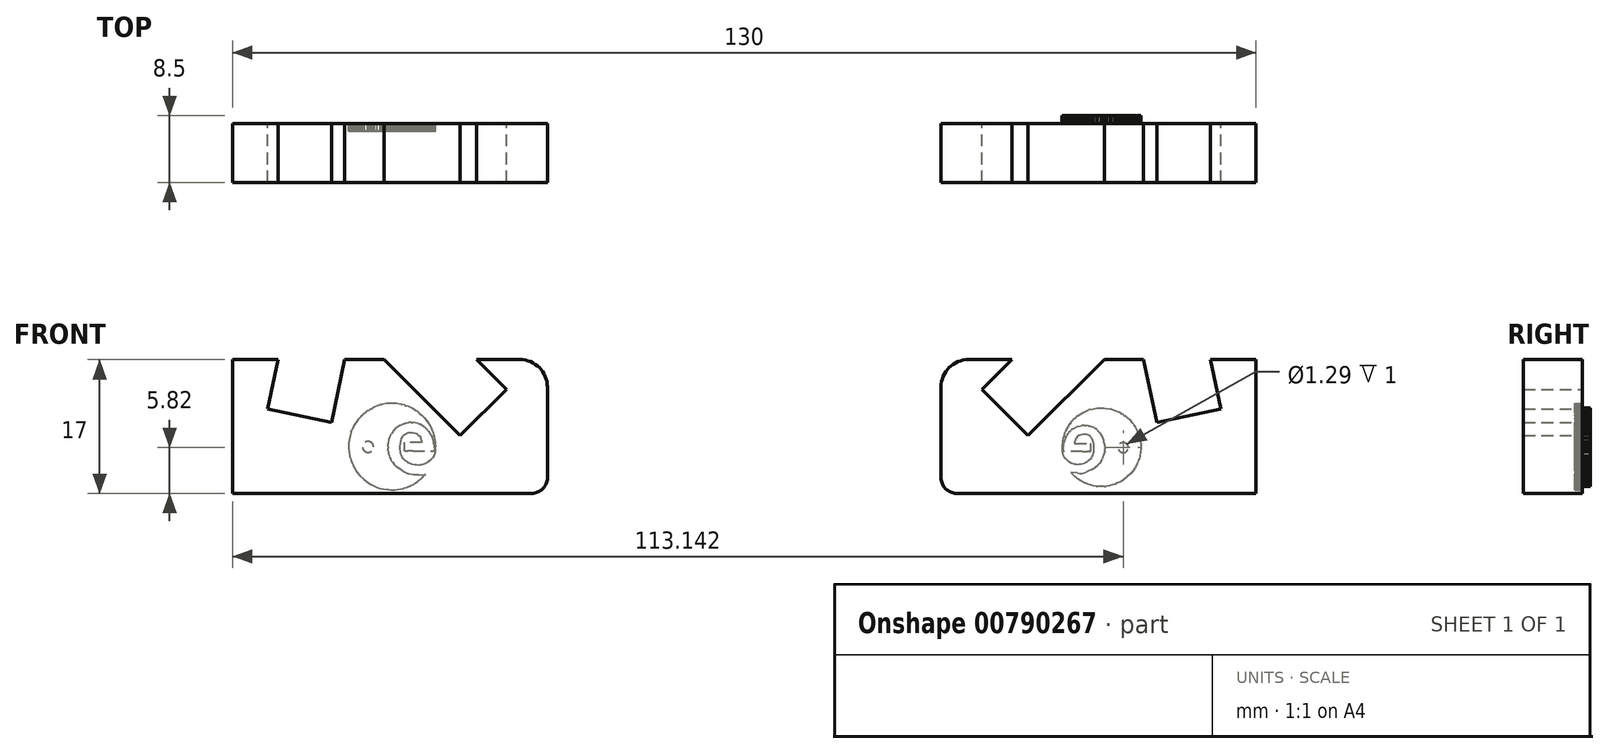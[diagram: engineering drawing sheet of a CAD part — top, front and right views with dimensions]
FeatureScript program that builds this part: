
annotation { "Feature Type Name" : "Feature", "Feature Type Description" : "" }
export const myFeature = defineFeature(function(context is Context, id is Id, definition is map)
    precondition{}
    {
        {
            var Q0;
            Q0=qCreatedBy(makeId("Front.planeOp"),FACE);
            var sketch = newSketch(context, id + "F0", { "sketchPlane" : qUnion([Q0])});
            skLineSegment(sketch, "E0", {"start": v(0, 0) * mm, "end": v(40, 0) * mm});
            skLineSegment(sketch, "E1", {"start": v(40, 0) * mm, "end": v(40, 17) * mm});
            skLineSegment(sketch, "E2", {"start": v(40, 17) * mm, "end": v(34.22, 17) * mm});
            skLineSegment(sketch, "E3", {"start": v(0, 17) * mm, "end": v(0, 0) * mm});
            skLineSegment(sketch, "E4", {"start": v(9, 17) * mm, "end": v(5.2, 13.2) * mm});
            skLineSegment(sketch, "E5", {"start": v(5.2, 13.2) * mm, "end": v(11.07, 7.33) * mm});
            skLineSegment(sketch, "E6", {"start": v(11.07, 7.33) * mm, "end": v(20.74, 17) * mm});
            skLineSegment(sketch, "E7", {"start": v(25.74, 17) * mm, "end": v(27.44, 9) * mm});
            skLineSegment(sketch, "E8", {"start": v(27.44, 9) * mm, "end": v(35.56, 10.73) * mm});
            skLineSegment(sketch, "E9", {"start": v(35.56, 10.73) * mm, "end": v(34.22, 17) * mm});
            skLineSegment(sketch, "E10.trimOffspring", {"start": v(9, 17) * mm, "end": v(0, 17) * mm});
            skLineSegment(sketch, "E11.trimOffspring", {"start": v(25.74, 17) * mm, "end": v(20.74, 17) * mm});
            skSolve(sketch);
        }
        {
            var Q0;
            Q0 = qSketchRegion(id + "F0", true);
            extrude(context, id + "F1", {"entities" : qUnion([Q0]), "depth" : 7.5 * mm, "offsetDistance" : 25 * mm});
        }
        {
            var Q0;
            Q0=makeQuery(id+"F1.opExtrude","SWEPT_EDGE",EDGE,{"disambiguationData":[OSD([sQuery(id+"F0.wireOp",EDGE,"E0"),sQuery(id+"F0.wireOp",EDGE,"E3")])]});
            fillet(context, id + "F2", {"entities" : qUnion([Q0]), "radius" : 2 * mm, "tangentPropagation" : true, "allowEdgeOverflow" : false});
        }
        {
            var Q0;
            Q0=makeQuery(id+"F1.opExtrude","SWEPT_EDGE",EDGE,{"disambiguationData":[OSD([sQuery(id+"F0.wireOp",EDGE,"E3"),sQuery(id+"F0.wireOp",EDGE,"E10.trimOffspring")])]});
            fillet(context, id + "F3", {"entities" : qUnion([Q0]), "radius" : 3.5 * mm, "tangentPropagation" : true, "allowEdgeOverflow" : false});
        }
        {
            var Q0;
            Q0=makeQuery(id+"F1.opExtrude","CAP_FACE",FACE,{"disambiguationData":[OSD([sQuery(id+"F0.wireOp",EDGE,"E0"),sQuery(id+"F0.wireOp",EDGE,"E1"),sQuery(id+"F0.wireOp",EDGE,"E2"),sQuery(id+"F0.wireOp",EDGE,"E3"),sQuery(id+"F0.wireOp",EDGE,"E4"),sQuery(id+"F0.wireOp",EDGE,"E5"),sQuery(id+"F0.wireOp",EDGE,"E6"),sQuery(id+"F0.wireOp",EDGE,"E7"),sQuery(id+"F0.wireOp",EDGE,"E8"),sQuery(id+"F0.wireOp",EDGE,"E9"),sQuery(id+"F0.wireOp",EDGE,"E10.trimOffspring"),sQuery(id+"F0.wireOp",EDGE,"E11.trimOffspring")])],"isStart":false});
            var sketch = newSketch(context, id + "F4", { "sketchPlane" : qUnion([Q0])});
            skSolve(sketch);
        }
        {
            var Q0;
            Q0=qCreatedBy(makeId("Right.planeOp"),FACE);
            cPlane(context, id + "F5", {"entities" : qUnion([Q0]), "cplaneType" : CPlaneType.OFFSET, "offset" : 25 * mm, "oppositeDirection" : true, "width" : 150 * mm, "height" : 150 * mm});
        }
        {
            var Q0;
            Q0=makeQuery(id+"F1.opExtrude","SWEPT_BODY",BODY,{"disambiguationData":[OSD([sQuery(id+"F0.wireOp",EDGE,"E0"),sQuery(id+"F0.wireOp",EDGE,"E1"),sQuery(id+"F0.wireOp",EDGE,"E2"),sQuery(id+"F0.wireOp",EDGE,"E3"),sQuery(id+"F0.wireOp",EDGE,"E4"),sQuery(id+"F0.wireOp",EDGE,"E5"),sQuery(id+"F0.wireOp",EDGE,"E6"),sQuery(id+"F0.wireOp",EDGE,"E7"),sQuery(id+"F0.wireOp",EDGE,"E8"),sQuery(id+"F0.wireOp",EDGE,"E9"),sQuery(id+"F0.wireOp",EDGE,"E10.trimOffspring"),sQuery(id+"F0.wireOp",EDGE,"E11.trimOffspring")])]});
            var Q1;
            Q1=qCreatedBy(id+"F5.planeOp",FACE);
            mirror(context, id + "F6", {"entities" : qUnion([Q0]), "mirrorPlane" : qUnion([Q1])});
        }
        {
            var Q0;
            {var subQ10=sQuery(id+"F0.wireOp",EDGE,"E1");Q0=makeQuery(id+"F4.imprint","IMPRINT",FACE,{"disambiguationData":[TD([[makeQuery(id+"F4.imprint","IMPRINT",EDGE,{"derivedFrom":makeQuery(id+"F1.opExtrude","CAP_EDGE",EDGE,{"disambiguationData":[OSD([subQ10])],"isStart":false})}),1.0]])]});}
            var sketch = newSketch(context, id + "F7", { "sketchPlane" : qUnion([Q0])});
            skLineSegment(sketch, "E12", {"start": v(15.48, 5.35) * mm, "end": v(15.48, 5.33) * mm});
            skLineSegment(sketch, "E13", {"start": v(24.52, 8.66) * mm, "end": v(24.53, 8.64) * mm});
            skLineSegment(sketch, "E14", {"start": v(24.56, 8.6) * mm, "end": v(24.53, 8.64) * mm});
            skLineSegment(sketch, "E15", {"start": v(24.56, 8.6) * mm, "end": v(24.56, 8.6) * mm});
            skLineSegment(sketch, "E16", {"start": v(24.7, 8.39) * mm, "end": v(24.78, 8.22) * mm});
            skLineSegment(sketch, "E17", {"start": v(24.56, 8.6) * mm, "end": v(24.7, 8.39) * mm});
            skLineSegment(sketch, "E18", {"start": v(24.78, 8.22) * mm, "end": v(24.8, 8.18) * mm});
            skLineSegment(sketch, "E19", {"start": v(24.8, 8.18) * mm, "end": v(24.84, 8.1) * mm});
            skLineSegment(sketch, "E20", {"start": v(24.84, 8.1) * mm, "end": v(24.9, 8) * mm});
            skLineSegment(sketch, "E21", {"start": v(24.9, 8) * mm, "end": v(24.91, 7.95) * mm});
            skLineSegment(sketch, "E22", {"start": v(24.91, 7.95) * mm, "end": v(24.95, 7.88) * mm});
            skLineSegment(sketch, "E23", {"start": v(24.95, 7.88) * mm, "end": v(24.97, 7.83) * mm});
            skLineSegment(sketch, "E24", {"start": v(25.1, 7.54) * mm, "end": v(24.97, 7.83) * mm});
            skLineSegment(sketch, "E25", {"start": v(25.1, 7.53) * mm, "end": v(25.1, 7.54) * mm});
            skLineSegment(sketch, "E26", {"start": v(25.24, 7.07) * mm, "end": v(25.33, 6.56) * mm});
            skLineSegment(sketch, "E27", {"start": v(25.1, 7.53) * mm, "end": v(25.24, 7.07) * mm});
            skLineSegment(sketch, "E28", {"start": v(25.38, 5.57) * mm, "end": v(25.36, 5.31) * mm});
            skLineSegment(sketch, "E29", {"start": v(25.38, 5.86) * mm, "end": v(25.38, 5.57) * mm});
            skLineSegment(sketch, "E30", {"start": v(25.36, 6.2) * mm, "end": v(25.38, 5.86) * mm});
            skLineSegment(sketch, "E31", {"start": v(25.33, 6.56) * mm, "end": v(25.36, 6.2) * mm});
            skLineSegment(sketch, "E32", {"start": v(25.36, 5.31) * mm, "end": v(25.24, 4.7) * mm});
            skLineSegment(sketch, "E33", {"start": v(25, 3.97) * mm, "end": v(24.9, 3.71) * mm});
            skLineSegment(sketch, "E34", {"start": v(25.1, 4.23) * mm, "end": v(25, 3.97) * mm});
            skLineSegment(sketch, "E35", {"start": v(25.18, 4.47) * mm, "end": v(25.1, 4.23) * mm});
            skLineSegment(sketch, "E36", {"start": v(25.24, 4.7) * mm, "end": v(25.18, 4.47) * mm});
            skLineSegment(sketch, "E37", {"start": v(24.9, 3.71) * mm, "end": v(24.86, 3.65) * mm});
            skLineSegment(sketch, "E38", {"start": v(23.62, 2.06) * mm, "end": v(23.08, 1.66) * mm});
            skLineSegment(sketch, "E39", {"start": v(24.1, 2.53) * mm, "end": v(23.62, 2.06) * mm});
            skLineSegment(sketch, "E40", {"start": v(24.4, 2.88) * mm, "end": v(24.1, 2.53) * mm});
            skLineSegment(sketch, "E41", {"start": v(24.64, 3.25) * mm, "end": v(24.4, 2.88) * mm});
            skLineSegment(sketch, "E42", {"start": v(24.86, 3.65) * mm, "end": v(24.64, 3.25) * mm});
            skLineSegment(sketch, "E43", {"start": v(21.36, 0.96) * mm, "end": v(20.93, 0.9) * mm});
            skLineSegment(sketch, "E44", {"start": v(21.73, 1.05) * mm, "end": v(21.36, 0.96) * mm});
            skLineSegment(sketch, "E45", {"start": v(22.09, 1.16) * mm, "end": v(21.73, 1.05) * mm});
            skLineSegment(sketch, "E46", {"start": v(22.42, 1.3) * mm, "end": v(22.09, 1.16) * mm});
            skLineSegment(sketch, "E47", {"start": v(22.76, 1.47) * mm, "end": v(22.42, 1.3) * mm});
            skLineSegment(sketch, "E48", {"start": v(23.08, 1.66) * mm, "end": v(22.76, 1.47) * mm});
            skLineSegment(sketch, "E49", {"start": v(20.77, 0.87) * mm, "end": v(20.93, 0.9) * mm});
            skLineSegment(sketch, "E50", {"start": v(20.79, 0.88) * mm, "end": v(20.77, 0.87) * mm});
            skLineSegment(sketch, "E51", {"start": v(20.79, 0.88) * mm, "end": v(20.46, 0.86) * mm});
            skLineSegment(sketch, "E52", {"start": v(20.09, 0.87) * mm, "end": v(19.8, 0.9) * mm});
            skLineSegment(sketch, "E53", {"start": v(20.46, 0.86) * mm, "end": v(20.09, 0.87) * mm});
            skLineSegment(sketch, "E54", {"start": v(19.76, 0.9) * mm, "end": v(19.8, 0.9) * mm});
            skLineSegment(sketch, "E55", {"start": v(19.76, 0.9) * mm, "end": v(19.76, 0.9) * mm});
            skLineSegment(sketch, "E56", {"start": v(19.38, 0.96) * mm, "end": v(19.02, 1.05) * mm});
            skLineSegment(sketch, "E57", {"start": v(19.76, 0.9) * mm, "end": v(19.38, 0.96) * mm});
            skLineSegment(sketch, "E58", {"start": v(18.96, 1.06) * mm, "end": v(19.02, 1.05) * mm});
            skLineSegment(sketch, "E59", {"start": v(18.96, 1.07) * mm, "end": v(18.96, 1.06) * mm});
            skLineSegment(sketch, "E60", {"start": v(18.7, 1.15) * mm, "end": v(18.44, 1.24) * mm});
            skLineSegment(sketch, "E61", {"start": v(18.96, 1.07) * mm, "end": v(18.7, 1.15) * mm});
            skLineSegment(sketch, "E62", {"start": v(18.44, 1.24) * mm, "end": v(18.41, 1.26) * mm});
            skLineSegment(sketch, "E63", {"start": v(18.41, 1.26) * mm, "end": v(18.27, 1.32) * mm});
            skLineSegment(sketch, "E64", {"start": v(18.27, 1.32) * mm, "end": v(18.25, 1.33) * mm});
            skLineSegment(sketch, "E65", {"start": v(18.25, 1.33) * mm, "end": v(18.23, 1.33) * mm});
            skLineSegment(sketch, "E66", {"start": v(18.23, 1.33) * mm, "end": v(18.15, 1.37) * mm});
            skLineSegment(sketch, "E67", {"start": v(18.15, 1.37) * mm, "end": v(17.9, 1.5) * mm});
            skLineSegment(sketch, "E68", {"start": v(17.9, 1.5) * mm, "end": v(17.89, 1.51) * mm});
            skLineSegment(sketch, "E69", {"start": v(17.89, 1.51) * mm, "end": v(17.82, 1.55) * mm});
            skLineSegment(sketch, "E70", {"start": v(17.82, 1.55) * mm, "end": v(17.78, 1.58) * mm});
            skLineSegment(sketch, "E71", {"start": v(17.78, 1.58) * mm, "end": v(17.65, 1.66) * mm});
            skLineSegment(sketch, "E72", {"start": v(17.65, 1.66) * mm, "end": v(17.4, 1.83) * mm});
            skLineSegment(sketch, "E73", {"start": v(17.28, 1.92) * mm, "end": v(17.19, 2) * mm});
            skLineSegment(sketch, "E74", {"start": v(17.4, 1.83) * mm, "end": v(17.28, 1.92) * mm});
            skLineSegment(sketch, "E75", {"start": v(17.19, 2) * mm, "end": v(17.18, 2) * mm});
            skLineSegment(sketch, "E76", {"start": v(17.05, 2.1) * mm, "end": v(16.96, 2.2) * mm});
            skLineSegment(sketch, "E77", {"start": v(17.18, 2) * mm, "end": v(17.05, 2.1) * mm});
            skLineSegment(sketch, "E78", {"start": v(16.84, 2.3) * mm, "end": v(16.96, 2.2) * mm});
            skLineSegment(sketch, "E79", {"start": v(16.85, 2.3) * mm, "end": v(16.84, 2.3) * mm});
            skLineSegment(sketch, "E80", {"start": v(16.85, 2.3) * mm, "end": v(16.67, 2.5) * mm});
            skLineSegment(sketch, "E81", {"start": v(16.66, 2.5) * mm, "end": v(16.67, 2.5) * mm});
            skLineSegment(sketch, "E82", {"start": v(16.52, 2.66) * mm, "end": v(16.66, 2.5) * mm});
            skLineSegment(sketch, "E83", {"start": v(17.31, 2.57) * mm, "end": v(16.52, 2.66) * mm});
            skLineSegment(sketch, "E84", {"start": v(18.17, 2.61) * mm, "end": v(18.48, 2.71) * mm});
            skLineSegment(sketch, "E85", {"start": v(17.9, 2.56) * mm, "end": v(18.17, 2.61) * mm});
            skLineSegment(sketch, "E86", {"start": v(17.62, 2.55) * mm, "end": v(17.9, 2.56) * mm});
            skLineSegment(sketch, "E87", {"start": v(17.31, 2.57) * mm, "end": v(17.62, 2.55) * mm});
            skLineSegment(sketch, "E88", {"start": v(19.16, 3.06) * mm, "end": v(18.48, 2.71) * mm});
            skLineSegment(sketch, "E89", {"start": v(19.16, 3.06) * mm, "end": v(19.34, 3.17) * mm});
            skLineSegment(sketch, "E90", {"start": v(19.34, 3.17) * mm, "end": v(19.55, 3.3) * mm});
            skLineSegment(sketch, "E91", {"start": v(19.55, 3.3) * mm, "end": v(19.59, 3.33) * mm});
            skLineSegment(sketch, "E92", {"start": v(19.59, 3.33) * mm, "end": v(19.59, 3.33) * mm});
            skLineSegment(sketch, "E93", {"start": v(19.59, 3.33) * mm, "end": v(19.6, 3.34) * mm});
            skLineSegment(sketch, "E94", {"start": v(19.6, 3.34) * mm, "end": v(19.6, 3.34) * mm});
            skLineSegment(sketch, "E95", {"start": v(19.84, 3.52) * mm, "end": v(20.01, 3.67) * mm});
            skLineSegment(sketch, "E96", {"start": v(19.6, 3.34) * mm, "end": v(19.84, 3.52) * mm});
            skLineSegment(sketch, "E97", {"start": v(20.01, 3.68) * mm, "end": v(20.01, 3.67) * mm});
            skLineSegment(sketch, "E98", {"start": v(20.13, 3.8) * mm, "end": v(20.01, 3.68) * mm});
            skLineSegment(sketch, "E99", {"start": v(20.32, 4.06) * mm, "end": v(20.13, 3.8) * mm});
            skLineSegment(sketch, "E100", {"start": v(20.35, 4.09) * mm, "end": v(20.32, 4.06) * mm});
            skLineSegment(sketch, "E101", {"start": v(20.35, 4.09) * mm, "end": v(20.51, 4.42) * mm});
            skLineSegment(sketch, "E102", {"start": v(20.58, 4.58) * mm, "end": v(20.51, 4.42) * mm});
            skLineSegment(sketch, "E103", {"start": v(20.58, 4.58) * mm, "end": v(20.58, 4.6) * mm});
            skLineSegment(sketch, "E104", {"start": v(20.68, 4.86) * mm, "end": v(20.74, 5.07) * mm});
            skLineSegment(sketch, "E105", {"start": v(20.58, 4.6) * mm, "end": v(20.68, 4.86) * mm});
            skLineSegment(sketch, "E106", {"start": v(20.74, 5.07) * mm, "end": v(20.75, 5.1) * mm});
            skLineSegment(sketch, "E107", {"start": v(20.8, 5.34) * mm, "end": v(20.75, 5.1) * mm});
            skLineSegment(sketch, "E108", {"start": v(20.8, 5.34) * mm, "end": v(20.83, 5.65) * mm});
            skLineSegment(sketch, "E109", {"start": v(20.83, 5.87) * mm, "end": v(20.83, 5.65) * mm});
            skLineSegment(sketch, "E110", {"start": v(20.81, 6.08) * mm, "end": v(20.79, 6.25) * mm});
            skLineSegment(sketch, "E111", {"start": v(20.83, 5.87) * mm, "end": v(20.81, 6.08) * mm});
            skLineSegment(sketch, "E112", {"start": v(20.79, 6.25) * mm, "end": v(20.79, 6.27) * mm});
            skLineSegment(sketch, "E113", {"start": v(20.79, 6.27) * mm, "end": v(20.79, 6.27) * mm});
            skLineSegment(sketch, "E114", {"start": v(20.79, 6.27) * mm, "end": v(20.71, 6.6) * mm});
            skLineSegment(sketch, "E115", {"start": v(20.71, 6.6) * mm, "end": v(20.68, 6.72) * mm});
            skLineSegment(sketch, "E116", {"start": v(20.68, 6.72) * mm, "end": v(20.57, 7.03) * mm});
            skLineSegment(sketch, "E117", {"start": v(20.48, 7.24) * mm, "end": v(20.4, 7.4) * mm});
            skLineSegment(sketch, "E118", {"start": v(20.57, 7.03) * mm, "end": v(20.48, 7.24) * mm});
            skLineSegment(sketch, "E119", {"start": v(20.27, 7.57) * mm, "end": v(20.4, 7.4) * mm});
            skLineSegment(sketch, "E120", {"start": v(20.27, 7.58) * mm, "end": v(20.27, 7.57) * mm});
            skLineSegment(sketch, "E121", {"start": v(20.17, 7.7) * mm, "end": v(20.08, 7.8) * mm});
            skLineSegment(sketch, "E122", {"start": v(20.27, 7.58) * mm, "end": v(20.17, 7.7) * mm});
            skLineSegment(sketch, "E123", {"start": v(20.08, 7.8) * mm, "end": v(19.88, 8) * mm});
            skLineSegment(sketch, "E124", {"start": v(19.78, 8.1) * mm, "end": v(19.88, 8) * mm});
            skLineSegment(sketch, "E125", {"start": v(19.78, 8.1) * mm, "end": v(19.59, 8.25) * mm});
            skLineSegment(sketch, "E126", {"start": v(19.5, 8.3) * mm, "end": v(19.59, 8.25) * mm});
            skLineSegment(sketch, "E127", {"start": v(19.27, 6.78) * mm, "end": v(19.25, 6.8) * mm});
            skLineSegment(sketch, "E128", {"start": v(19.25, 6.8) * mm, "end": v(19.17, 6.97) * mm});
            skLineSegment(sketch, "E129", {"start": v(19.17, 6.97) * mm, "end": v(19.07, 7.12) * mm});
            skLineSegment(sketch, "E130", {"start": v(19.07, 7.12) * mm, "end": v(18.95, 7.24) * mm});
            skLineSegment(sketch, "E131", {"start": v(18.95, 7.24) * mm, "end": v(18.8, 7.34) * mm});
            skLineSegment(sketch, "E132", {"start": v(18.8, 7.34) * mm, "end": v(18.65, 7.41) * mm});
            skLineSegment(sketch, "E133", {"start": v(18.65, 7.41) * mm, "end": v(18.48, 7.46) * mm});
            skLineSegment(sketch, "E134", {"start": v(18.48, 7.46) * mm, "end": v(18.11, 7.5) * mm});
            skLineSegment(sketch, "E135", {"start": v(18.11, 7.5) * mm, "end": v(18.06, 7.5) * mm});
            skLineSegment(sketch, "E136", {"start": v(18.06, 7.5) * mm, "end": v(18, 7.5) * mm});
            skLineSegment(sketch, "E137", {"start": v(18, 7.5) * mm, "end": v(17.78, 7.45) * mm});
            skLineSegment(sketch, "E138", {"start": v(17.78, 7.45) * mm, "end": v(17.57, 7.37) * mm});
            skLineSegment(sketch, "E139", {"start": v(17.57, 7.37) * mm, "end": v(17.55, 7.36) * mm});
            skLineSegment(sketch, "E140", {"start": v(17.55, 7.36) * mm, "end": v(17.55, 7.36) * mm});
            skLineSegment(sketch, "E141", {"start": v(17.55, 7.36) * mm, "end": v(17.35, 7.23) * mm});
            skLineSegment(sketch, "E142", {"start": v(17.35, 7.23) * mm, "end": v(17.2, 7.07) * mm});
            skLineSegment(sketch, "E143", {"start": v(17.2, 7.07) * mm, "end": v(17.08, 6.89) * mm});
            skLineSegment(sketch, "E144", {"start": v(17.08, 6.89) * mm, "end": v(17.08, 6.88) * mm});
            skLineSegment(sketch, "E145", {"start": v(17.08, 6.88) * mm, "end": v(17.05, 6.82) * mm});
            skLineSegment(sketch, "E146", {"start": v(17.05, 6.82) * mm, "end": v(17, 6.68) * mm});
            skLineSegment(sketch, "E147", {"start": v(17, 6.68) * mm, "end": v(17, 6.68) * mm});
            skLineSegment(sketch, "E148", {"start": v(17, 6.68) * mm, "end": v(16.96, 6.5) * mm});
            skLineSegment(sketch, "E149", {"start": v(16.96, 6.5) * mm, "end": v(16.95, 6.5) * mm});
            skLineSegment(sketch, "E150", {"start": v(16.95, 6.66) * mm, "end": v(16.95, 6.33) * mm});
            skLineSegment(sketch, "E151", {"start": v(16.95, 6.33) * mm, "end": v(18.98, 6.33) * mm});
            skLineSegment(sketch, "E152", {"start": v(18.98, 6.33) * mm, "end": v(18.98, 5.33) * mm});
            skLineSegment(sketch, "E153", {"start": v(18.88, 5.33) * mm, "end": v(18.98, 5.33) * mm});
            skLineSegment(sketch, "E154", {"start": v(18.88, 5.33) * mm, "end": v(18.57, 5.33) * mm});
            skLineSegment(sketch, "E155", {"start": v(18.57, 5.33) * mm, "end": v(18.57, 5.33) * mm});
            skLineSegment(sketch, "E156", {"start": v(17.99, 5.33) * mm, "end": v(18.57, 5.33) * mm});
            skLineSegment(sketch, "E157", {"start": v(17.99, 5.33) * mm, "end": v(18, 5.33) * mm});
            skLineSegment(sketch, "E158", {"start": v(18, 5.33) * mm, "end": v(15.48, 5.33) * mm});
            skLineSegment(sketch, "E159", {"start": v(15.48, 5.35) * mm, "end": v(15.47, 5.55) * mm});
            skLineSegment(sketch, "E160", {"start": v(15.5, 5.81) * mm, "end": v(15.48, 5.66) * mm});
            skLineSegment(sketch, "E161", {"start": v(15.48, 5.66) * mm, "end": v(15.47, 5.55) * mm});
            skLineSegment(sketch, "E162", {"start": v(15.53, 6.08) * mm, "end": v(15.5, 5.81) * mm});
            skLineSegment(sketch, "E163", {"start": v(15.53, 6.08) * mm, "end": v(15.53, 6.08) * mm});
            skLineSegment(sketch, "E164", {"start": v(15.53, 6.08) * mm, "end": v(15.56, 6.27) * mm});
            skLineSegment(sketch, "E165", {"start": v(15.58, 6.33) * mm, "end": v(15.56, 6.27) * mm});
            skLineSegment(sketch, "E166", {"start": v(15.62, 6.5) * mm, "end": v(15.58, 6.33) * mm});
            skLineSegment(sketch, "E167", {"start": v(15.65, 6.58) * mm, "end": v(15.62, 6.5) * mm});
            skLineSegment(sketch, "E168", {"start": v(15.65, 6.6) * mm, "end": v(15.65, 6.58) * mm});
            skLineSegment(sketch, "E169", {"start": v(15.65, 6.6) * mm, "end": v(15.65, 6.6) * mm});
            skLineSegment(sketch, "E170", {"start": v(15.66, 6.64) * mm, "end": v(15.65, 6.6) * mm});
            skLineSegment(sketch, "E171", {"start": v(15.67, 6.65) * mm, "end": v(15.66, 6.64) * mm});
            skLineSegment(sketch, "E172", {"start": v(15.7, 6.73) * mm, "end": v(15.67, 6.65) * mm});
            skLineSegment(sketch, "E173", {"start": v(15.77, 6.96) * mm, "end": v(15.72, 6.83) * mm});
            skLineSegment(sketch, "E174", {"start": v(15.72, 6.83) * mm, "end": v(15.7, 6.73) * mm});
            skLineSegment(sketch, "E175", {"start": v(15.77, 6.96) * mm, "end": v(15.77, 6.96) * mm});
            skLineSegment(sketch, "E176", {"start": v(18.2, 8.64) * mm, "end": v(18.2, 8.64) * mm});
            skLineSegment(sketch, "E177", {"start": v(24.25, 9.02) * mm, "end": v(24.26, 9) * mm});
            skLineSegment(sketch, "E178", {"start": v(18.2, 8.64) * mm, "end": v(18.45, 8.63) * mm});
            skLineSegment(sketch, "E179", {"start": v(24.25, 9.02) * mm, "end": v(24.25, 9.02) * mm});
            skLineSegment(sketch, "E180", {"start": v(18.72, 8.58) * mm, "end": v(18.45, 8.63) * mm});
            skLineSegment(sketch, "E181", {"start": v(24.25, 9.02) * mm, "end": v(24.18, 9.1) * mm});
            skLineSegment(sketch, "E182", {"start": v(18.72, 8.58) * mm, "end": v(18.88, 8.54) * mm});
            skLineSegment(sketch, "E183", {"start": v(23.91, 9.39) * mm, "end": v(24.18, 9.1) * mm});
            skLineSegment(sketch, "E184", {"start": v(19.2, 8.43) * mm, "end": v(18.99, 8.51) * mm});
            skLineSegment(sketch, "E185", {"start": v(23.91, 9.39) * mm, "end": v(23.92, 9.4) * mm});
            skLineSegment(sketch, "E186", {"start": v(23.92, 9.4) * mm, "end": v(23.8, 9.5) * mm});
            skLineSegment(sketch, "E187", {"start": v(24.4, 8.81) * mm, "end": v(24.52, 8.66) * mm});
            skLineSegment(sketch, "E188", {"start": v(19.5, 8.3) * mm, "end": v(19.34, 8.38) * mm});
            skLineSegment(sketch, "E189", {"start": v(23.56, 9.7) * mm, "end": v(23.7, 9.6) * mm});
            skLineSegment(sketch, "E190", {"start": v(23.7, 9.6) * mm, "end": v(23.8, 9.5) * mm});
            skLineSegment(sketch, "E191", {"start": v(23.54, 9.71) * mm, "end": v(23.56, 9.7) * mm});
            skLineSegment(sketch, "E192", {"start": v(23.54, 9.71) * mm, "end": v(23.54, 9.71) * mm});
            skLineSegment(sketch, "E193", {"start": v(23.54, 9.71) * mm, "end": v(23.35, 9.85) * mm});
            skLineSegment(sketch, "E194", {"start": v(22.6, 10.33) * mm, "end": v(22.6, 10.33) * mm});
            skLineSegment(sketch, "E195", {"start": v(22.12, 10.54) * mm, "end": v(22.4, 10.43) * mm});
            skLineSegment(sketch, "E196", {"start": v(21.6, 10.7) * mm, "end": v(22.12, 10.54) * mm});
            skLineSegment(sketch, "E197", {"start": v(22.8, 10.22) * mm, "end": v(22.6, 10.33) * mm});
            skLineSegment(sketch, "E198", {"start": v(22.8, 10.22) * mm, "end": v(22.8, 10.22) * mm});
            skLineSegment(sketch, "E199", {"start": v(22.8, 10.22) * mm, "end": v(22.99, 10.1) * mm});
            skLineSegment(sketch, "E200", {"start": v(23.18, 10) * mm, "end": v(22.99, 10.1) * mm});
            skLineSegment(sketch, "E201", {"start": v(23.18, 9.98) * mm, "end": v(23.18, 10) * mm});
            skLineSegment(sketch, "E202", {"start": v(23.18, 9.98) * mm, "end": v(23.35, 9.85) * mm});
            skLineSegment(sketch, "E203", {"start": v(18.99, 8.51) * mm, "end": v(18.88, 8.54) * mm});
            skLineSegment(sketch, "E204", {"start": v(24.26, 9) * mm, "end": v(24.4, 8.81) * mm});
            skLineSegment(sketch, "E205", {"start": v(18.2, 8.64) * mm, "end": v(17.93, 8.63) * mm});
            skLineSegment(sketch, "E206", {"start": v(22.4, 10.43) * mm, "end": v(22.6, 10.33) * mm});
            skCircle(sketch, "E207", {"center": v(23.14, 5.82) * mm, "radius": 0.64 * mm});
            skLineSegment(sketch, "E208", {"start": v(19.18, 4.64) * mm, "end": v(19.29, 4.85) * mm});
            skLineSegment(sketch, "E209", {"start": v(17.39, 8.52) * mm, "end": v(17.93, 8.63) * mm});
            skLineSegment(sketch, "E210", {"start": v(17.39, 8.52) * mm, "end": v(17.2, 8.45) * mm});
            skLineSegment(sketch, "E211", {"start": v(16.73, 8.2) * mm, "end": v(17.2, 8.45) * mm});
            skLineSegment(sketch, "E212", {"start": v(16.6, 8.1) * mm, "end": v(16.5, 8.02) * mm});
            skLineSegment(sketch, "E213", {"start": v(16.73, 8.2) * mm, "end": v(16.6, 8.1) * mm});
            skLineSegment(sketch, "E214", {"start": v(16.3, 7.84) * mm, "end": v(16.5, 8.02) * mm});
            skLineSegment(sketch, "E215", {"start": v(16.3, 7.84) * mm, "end": v(16.3, 7.84) * mm});
            skLineSegment(sketch, "E216", {"start": v(16.3, 7.84) * mm, "end": v(16.27, 7.8) * mm});
            skLineSegment(sketch, "E217", {"start": v(16.18, 7.68) * mm, "end": v(16.12, 7.6) * mm});
            skLineSegment(sketch, "E218", {"start": v(16.27, 7.8) * mm, "end": v(16.18, 7.68) * mm});
            skLineSegment(sketch, "E219", {"start": v(16.12, 7.6) * mm, "end": v(15.96, 7.33) * mm});
            skLineSegment(sketch, "E220", {"start": v(15.87, 7.17) * mm, "end": v(15.96, 7.33) * mm});
            skLineSegment(sketch, "E221", {"start": v(15.87, 7.17) * mm, "end": v(15.86, 7.15) * mm});
            skLineSegment(sketch, "E222", {"start": v(15.86, 7.15) * mm, "end": v(15.77, 6.96) * mm});
            skLineSegment(sketch, "E223", {"start": v(19.26, 6.78) * mm, "end": v(19.27, 6.78) * mm});
            skLineSegment(sketch, "E224", {"start": v(19.33, 6.58) * mm, "end": v(19.26, 6.78) * mm});
            skLineSegment(sketch, "E225", {"start": v(19.33, 6.59) * mm, "end": v(19.33, 6.58) * mm});
            skLineSegment(sketch, "E226", {"start": v(19.34, 6.53) * mm, "end": v(19.33, 6.59) * mm});
            skLineSegment(sketch, "E227", {"start": v(19.4, 6.2) * mm, "end": v(19.34, 6.53) * mm});
            skLineSegment(sketch, "E228", {"start": v(15.5, 6.96) * mm, "end": v(15.44, 6.71) * mm});
            skLineSegment(sketch, "E229", {"start": v(15.51, 7.08) * mm, "end": v(15.5, 6.96) * mm});
            skLineSegment(sketch, "E230", {"start": v(15.52, 7.07) * mm, "end": v(15.51, 7.08) * mm});
            skLineSegment(sketch, "E231", {"start": v(15.7, 7.65) * mm, "end": v(15.52, 7.07) * mm});
            skLineSegment(sketch, "E232", {"start": v(15.72, 7.71) * mm, "end": v(15.7, 7.65) * mm});
            skLineSegment(sketch, "E233", {"start": v(15.8, 7.88) * mm, "end": v(15.72, 7.71) * mm});
            skLineSegment(sketch, "E234", {"start": v(15.8, 7.9) * mm, "end": v(15.8, 7.88) * mm});
            skLineSegment(sketch, "E235", {"start": v(15.8, 7.9) * mm, "end": v(15.8, 7.9) * mm});
            skLineSegment(sketch, "E236", {"start": v(16, 8.27) * mm, "end": v(15.8, 7.9) * mm});
            skLineSegment(sketch, "E237", {"start": v(16, 8.27) * mm, "end": v(16, 8.27) * mm});
            skLineSegment(sketch, "E238", {"start": v(16, 8.3) * mm, "end": v(16, 8.27) * mm});
            skLineSegment(sketch, "E239", {"start": v(16.03, 8.33) * mm, "end": v(16, 8.3) * mm});
            skLineSegment(sketch, "E240", {"start": v(16.19, 8.58) * mm, "end": v(16.03, 8.33) * mm});
            skLineSegment(sketch, "E241", {"start": v(16.21, 8.62) * mm, "end": v(16.19, 8.58) * mm});
            skLineSegment(sketch, "E242", {"start": v(16.23, 8.64) * mm, "end": v(16.21, 8.62) * mm});
            skLineSegment(sketch, "E243", {"start": v(16.21, 8.64) * mm, "end": v(16.23, 8.64) * mm});
            skLineSegment(sketch, "E244", {"start": v(16.34, 8.82) * mm, "end": v(16.21, 8.64) * mm});
            skLineSegment(sketch, "E245", {"start": v(16.36, 8.82) * mm, "end": v(16.34, 8.82) * mm});
            skLineSegment(sketch, "E246", {"start": v(16.48, 8.98) * mm, "end": v(16.36, 8.82) * mm});
            skLineSegment(sketch, "E247", {"start": v(16.47, 8.98) * mm, "end": v(16.48, 8.98) * mm});
            skLineSegment(sketch, "E248", {"start": v(16.62, 9.15) * mm, "end": v(16.47, 8.98) * mm});
            skLineSegment(sketch, "E249", {"start": v(16.7, 9.26) * mm, "end": v(16.62, 9.15) * mm});
            skLineSegment(sketch, "E250", {"start": v(16.75, 9.3) * mm, "end": v(16.7, 9.26) * mm});
            skLineSegment(sketch, "E251", {"start": v(16.8, 9.36) * mm, "end": v(16.75, 9.3) * mm});
            skLineSegment(sketch, "E252", {"start": v(18.93, 10.64) * mm, "end": v(19.28, 10.73) * mm});
            skLineSegment(sketch, "E253", {"start": v(19.3, 10.74) * mm, "end": v(19.28, 10.73) * mm});
            skLineSegment(sketch, "E254", {"start": v(19.3, 10.73) * mm, "end": v(19.3, 10.74) * mm});
            skLineSegment(sketch, "E255", {"start": v(19.83, 10.83) * mm, "end": v(20.36, 10.86) * mm});
            skLineSegment(sketch, "E256", {"start": v(19.3, 10.73) * mm, "end": v(19.83, 10.83) * mm});
            skLineSegment(sketch, "E257", {"start": v(20.7, 10.84) * mm, "end": v(20.98, 10.82) * mm});
            skLineSegment(sketch, "E258", {"start": v(21.6, 10.7) * mm, "end": v(21.6, 10.7) * mm});
            skLineSegment(sketch, "E259", {"start": v(21.6, 10.7) * mm, "end": v(21.54, 10.71) * mm});
            skLineSegment(sketch, "E260", {"start": v(20.98, 10.82) * mm, "end": v(21.54, 10.71) * mm});
            skLineSegment(sketch, "E261", {"start": v(20.36, 10.86) * mm, "end": v(20.7, 10.84) * mm});
            skLineSegment(sketch, "E262", {"start": v(18.93, 10.64) * mm, "end": v(18.93, 10.64) * mm});
            skLineSegment(sketch, "E263", {"start": v(18.93, 10.64) * mm, "end": v(18.73, 10.58) * mm});
            skLineSegment(sketch, "E264", {"start": v(18.23, 10.37) * mm, "end": v(18.47, 10.48) * mm});
            skLineSegment(sketch, "E265", {"start": v(18.47, 10.48) * mm, "end": v(18.73, 10.58) * mm});
            skLineSegment(sketch, "E266", {"start": v(17.76, 10.1) * mm, "end": v(18.02, 10.26) * mm});
            skLineSegment(sketch, "E267", {"start": v(18.02, 10.26) * mm, "end": v(18.23, 10.37) * mm});
            skLineSegment(sketch, "E268", {"start": v(17.76, 10.1) * mm, "end": v(17.65, 10.04) * mm});
            skLineSegment(sketch, "E269", {"start": v(17.65, 10.04) * mm, "end": v(17.65, 10.04) * mm});
            skLineSegment(sketch, "E270", {"start": v(17.45, 9.9) * mm, "end": v(17.65, 10.04) * mm});
            skLineSegment(sketch, "E271", {"start": v(17.45, 9.9) * mm, "end": v(17.2, 9.7) * mm});
            skLineSegment(sketch, "E272", {"start": v(17.2, 9.7) * mm, "end": v(16.98, 9.51) * mm});
            skLineSegment(sketch, "E273", {"start": v(16.98, 9.51) * mm, "end": v(16.8, 9.36) * mm});
            skLineSegment(sketch, "E274", {"start": v(15.44, 6.71) * mm, "end": v(15.44, 6.71) * mm});
            skLineSegment(sketch, "E275", {"start": v(15.44, 6.71) * mm, "end": v(15.43, 6.67) * mm});
            skLineSegment(sketch, "E276", {"start": v(15.43, 6.67) * mm, "end": v(15.4, 6.38) * mm});
            skLineSegment(sketch, "E277", {"start": v(15.4, 6.38) * mm, "end": v(15.37, 6.15) * mm});
            skLineSegment(sketch, "E278", {"start": v(15.37, 6.15) * mm, "end": v(15.37, 5.89) * mm});
            skLineSegment(sketch, "E279", {"start": v(15.37, 5.89) * mm, "end": v(15.37, 5.74) * mm});
            skLineSegment(sketch, "E280", {"start": v(15.37, 5.74) * mm, "end": v(15.37, 5.63) * mm});
            skLineSegment(sketch, "E281", {"start": v(15.37, 5.63) * mm, "end": v(15.37, 5.63) * mm});
            skLineSegment(sketch, "E282", {"start": v(15.37, 5.63) * mm, "end": v(15.38, 5.37) * mm});
            skLineSegment(sketch, "E283", {"start": v(15.38, 5.37) * mm, "end": v(15.4, 5.22) * mm});
            skLineSegment(sketch, "E284", {"start": v(15.4, 5.22) * mm, "end": v(15.42, 5.1) * mm});
            skLineSegment(sketch, "E285", {"start": v(15.42, 5.1) * mm, "end": v(15.42, 5.1) * mm});
            skLineSegment(sketch, "E286", {"start": v(15.42, 5.1) * mm, "end": v(15.43, 5.07) * mm});
            skLineSegment(sketch, "E287", {"start": v(15.43, 5.07) * mm, "end": v(15.46, 4.96) * mm});
            skLineSegment(sketch, "E288", {"start": v(15.46, 4.96) * mm, "end": v(15.5, 4.87) * mm});
            skLineSegment(sketch, "E289", {"start": v(15.5, 4.87) * mm, "end": v(15.5, 4.86) * mm});
            skLineSegment(sketch, "E290", {"start": v(15.5, 4.86) * mm, "end": v(15.63, 4.64) * mm});
            skLineSegment(sketch, "E291", {"start": v(15.63, 4.64) * mm, "end": v(15.7, 4.51) * mm});
            skLineSegment(sketch, "E292", {"start": v(15.7, 4.51) * mm, "end": v(15.73, 4.48) * mm});
            skLineSegment(sketch, "E293", {"start": v(15.73, 4.48) * mm, "end": v(15.74, 4.48) * mm});
            skLineSegment(sketch, "E294", {"start": v(15.74, 4.48) * mm, "end": v(15.98, 4.23) * mm});
            skLineSegment(sketch, "E295", {"start": v(15.98, 4.23) * mm, "end": v(16.2, 4.07) * mm});
            skLineSegment(sketch, "E296", {"start": v(16.2, 4.07) * mm, "end": v(16.23, 4.04) * mm});
            skLineSegment(sketch, "E297", {"start": v(16.23, 4.04) * mm, "end": v(16.25, 4.03) * mm});
            skLineSegment(sketch, "E298", {"start": v(16.25, 4.03) * mm, "end": v(16.25, 4.03) * mm});
            skLineSegment(sketch, "E299", {"start": v(16.25, 4.03) * mm, "end": v(16.6, 3.85) * mm});
            skLineSegment(sketch, "E300", {"start": v(16.6, 3.85) * mm, "end": v(16.75, 3.8) * mm});
            skLineSegment(sketch, "E301", {"start": v(16.75, 3.8) * mm, "end": v(16.93, 3.75) * mm});
            skLineSegment(sketch, "E302", {"start": v(16.93, 3.75) * mm, "end": v(17.04, 3.73) * mm});
            skLineSegment(sketch, "E303", {"start": v(17.04, 3.73) * mm, "end": v(17.12, 3.72) * mm});
            skLineSegment(sketch, "E304", {"start": v(17.12, 3.72) * mm, "end": v(17.27, 3.7) * mm});
            skLineSegment(sketch, "E305", {"start": v(17.27, 3.7) * mm, "end": v(17.54, 3.7) * mm});
            skLineSegment(sketch, "E306", {"start": v(17.54, 3.7) * mm, "end": v(17.72, 3.73) * mm});
            skLineSegment(sketch, "E307", {"start": v(17.72, 3.73) * mm, "end": v(17.77, 3.74) * mm});
            skLineSegment(sketch, "E308", {"start": v(17.77, 3.74) * mm, "end": v(18.05, 3.8) * mm});
            skLineSegment(sketch, "E309", {"start": v(18.05, 3.8) * mm, "end": v(18.3, 3.9) * mm});
            skLineSegment(sketch, "E310", {"start": v(18.3, 3.9) * mm, "end": v(18.31, 3.9) * mm});
            skLineSegment(sketch, "E311", {"start": v(18.31, 3.9) * mm, "end": v(18.5, 4) * mm});
            skLineSegment(sketch, "E312", {"start": v(18.5, 4) * mm, "end": v(18.5, 4) * mm});
            skLineSegment(sketch, "E313", {"start": v(18.5, 4) * mm, "end": v(18.6, 4.05) * mm});
            skLineSegment(sketch, "E314", {"start": v(18.6, 4.05) * mm, "end": v(18.8, 4.22) * mm});
            skLineSegment(sketch, "E315", {"start": v(18.8, 4.22) * mm, "end": v(19.08, 4.5) * mm});
            skLineSegment(sketch, "E316", {"start": v(19.08, 4.5) * mm, "end": v(19.1, 4.51) * mm});
            skLineSegment(sketch, "E317", {"start": v(19.1, 4.51) * mm, "end": v(19.18, 4.64) * mm});
            skLineSegment(sketch, "E318", {"start": v(19.29, 4.85) * mm, "end": v(19.36, 5.07) * mm});
            skLineSegment(sketch, "E319", {"start": v(19.36, 5.07) * mm, "end": v(19.4, 5.3) * mm});
            skLineSegment(sketch, "E320", {"start": v(19.4, 5.3) * mm, "end": v(19.43, 5.53) * mm});
            skLineSegment(sketch, "E321", {"start": v(19.43, 5.53) * mm, "end": v(19.43, 5.86) * mm});
            skLineSegment(sketch, "E322", {"start": v(19.43, 5.86) * mm, "end": v(19.4, 6.2) * mm});
            skLineSegment(sketch, "E323", {"start": v(19.34, 8.38) * mm, "end": v(19.2, 8.43) * mm});
            skSolve(sketch);
        }
        {
            var Q0;
            Q0 = qSketchRegion(id + "F7", true);
            extrude(context, id + "F8", {"entities" : qUnion([Q0]), "operationType" : NewBodyOperationType.ADD, "oppositeDirection" : true, "depth" : 8.5 * mm, "offsetDistance" : 25 * mm});
        }
        {
            var Q0;
            Q0=makeQuery(id+"F6.opPattern","COPY",FACE,{"derivedFrom":makeQuery(id+"F1.opExtrude","CAP_FACE",FACE,{"disambiguationData":[OSD([sQuery(id+"F0.wireOp",EDGE,"E0"),sQuery(id+"F0.wireOp",EDGE,"E1"),sQuery(id+"F0.wireOp",EDGE,"E2"),sQuery(id+"F0.wireOp",EDGE,"E3"),sQuery(id+"F0.wireOp",EDGE,"E4"),sQuery(id+"F0.wireOp",EDGE,"E5"),sQuery(id+"F0.wireOp",EDGE,"E6"),sQuery(id+"F0.wireOp",EDGE,"E7"),sQuery(id+"F0.wireOp",EDGE,"E8"),sQuery(id+"F0.wireOp",EDGE,"E9"),sQuery(id+"F0.wireOp",EDGE,"E10.trimOffspring"),sQuery(id+"F0.wireOp",EDGE,"E11.trimOffspring")])],"isStart":true}),"instanceName":"1"});
            var sketch = newSketch(context, id + "F9", { "sketchPlane" : qUnion([Q0])});
            skLineSegment(sketch, "E324", {"start": v(64.36, 5.4) * mm, "end": v(64.36, 5.37) * mm});
            skLineSegment(sketch, "E325", {"start": v(74.3, 9.03) * mm, "end": v(74.32, 9) * mm});
            skLineSegment(sketch, "E326", {"start": v(74.35, 8.96) * mm, "end": v(74.32, 9) * mm});
            skLineSegment(sketch, "E327", {"start": v(74.35, 8.96) * mm, "end": v(74.35, 8.96) * mm});
            skLineSegment(sketch, "E328", {"start": v(74.5, 8.73) * mm, "end": v(74.6, 8.55) * mm});
            skLineSegment(sketch, "E329", {"start": v(74.35, 8.96) * mm, "end": v(74.5, 8.73) * mm});
            skLineSegment(sketch, "E330", {"start": v(74.6, 8.55) * mm, "end": v(74.62, 8.5) * mm});
            skLineSegment(sketch, "E331", {"start": v(74.62, 8.5) * mm, "end": v(74.66, 8.42) * mm});
            skLineSegment(sketch, "E332", {"start": v(74.66, 8.42) * mm, "end": v(74.71, 8.3) * mm});
            skLineSegment(sketch, "E333", {"start": v(74.71, 8.3) * mm, "end": v(74.74, 8.25) * mm});
            skLineSegment(sketch, "E334", {"start": v(74.74, 8.25) * mm, "end": v(74.77, 8.17) * mm});
            skLineSegment(sketch, "E335", {"start": v(74.77, 8.17) * mm, "end": v(74.8, 8.12) * mm});
            skLineSegment(sketch, "E336", {"start": v(74.94, 7.8) * mm, "end": v(74.8, 8.12) * mm});
            skLineSegment(sketch, "E337", {"start": v(74.93, 7.79) * mm, "end": v(74.94, 7.8) * mm});
            skLineSegment(sketch, "E338", {"start": v(75.1, 7.27) * mm, "end": v(75.2, 6.72) * mm});
            skLineSegment(sketch, "E339", {"start": v(74.93, 7.79) * mm, "end": v(75.1, 7.27) * mm});
            skLineSegment(sketch, "E340", {"start": v(75.25, 5.63) * mm, "end": v(75.22, 5.35) * mm});
            skLineSegment(sketch, "E341", {"start": v(75.25, 5.95) * mm, "end": v(75.25, 5.63) * mm});
            skLineSegment(sketch, "E342", {"start": v(75.23, 6.33) * mm, "end": v(75.25, 5.95) * mm});
            skLineSegment(sketch, "E343", {"start": v(75.2, 6.72) * mm, "end": v(75.23, 6.33) * mm});
            skLineSegment(sketch, "E344", {"start": v(75.22, 5.35) * mm, "end": v(75.1, 4.68) * mm});
            skLineSegment(sketch, "E345", {"start": v(74.84, 3.87) * mm, "end": v(74.71, 3.59) * mm});
            skLineSegment(sketch, "E346", {"start": v(74.95, 4.15) * mm, "end": v(74.84, 3.87) * mm});
            skLineSegment(sketch, "E347", {"start": v(75.03, 4.42) * mm, "end": v(74.95, 4.15) * mm});
            skLineSegment(sketch, "E348", {"start": v(75.1, 4.68) * mm, "end": v(75.03, 4.42) * mm});
            skLineSegment(sketch, "E349", {"start": v(74.71, 3.59) * mm, "end": v(74.68, 3.52) * mm});
            skLineSegment(sketch, "E350", {"start": v(73.32, 1.77) * mm, "end": v(72.72, 1.32) * mm});
            skLineSegment(sketch, "E351", {"start": v(73.85, 2.28) * mm, "end": v(73.32, 1.77) * mm});
            skLineSegment(sketch, "E352", {"start": v(74.16, 2.67) * mm, "end": v(73.85, 2.28) * mm});
            skLineSegment(sketch, "E353", {"start": v(74.44, 3.08) * mm, "end": v(74.16, 2.67) * mm});
            skLineSegment(sketch, "E354", {"start": v(74.68, 3.52) * mm, "end": v(74.44, 3.08) * mm});
            skLineSegment(sketch, "E355", {"start": v(70.83, 0.56) * mm, "end": v(70.36, 0.5) * mm});
            skLineSegment(sketch, "E356", {"start": v(71.24, 0.65) * mm, "end": v(70.83, 0.56) * mm});
            skLineSegment(sketch, "E357", {"start": v(71.63, 0.78) * mm, "end": v(71.24, 0.65) * mm});
            skLineSegment(sketch, "E358", {"start": v(72, 0.94) * mm, "end": v(71.63, 0.78) * mm});
            skLineSegment(sketch, "E359", {"start": v(72.37, 1.12) * mm, "end": v(72, 0.94) * mm});
            skLineSegment(sketch, "E360", {"start": v(72.72, 1.32) * mm, "end": v(72.37, 1.12) * mm});
            skLineSegment(sketch, "E361", {"start": v(70.18, 0.46) * mm, "end": v(70.36, 0.5) * mm});
            skLineSegment(sketch, "E362", {"start": v(70.2, 0.47) * mm, "end": v(70.18, 0.46) * mm});
            skLineSegment(sketch, "E363", {"start": v(70.2, 0.47) * mm, "end": v(69.84, 0.45) * mm});
            skLineSegment(sketch, "E364", {"start": v(69.43, 0.46) * mm, "end": v(69.1, 0.48) * mm});
            skLineSegment(sketch, "E365", {"start": v(69.84, 0.45) * mm, "end": v(69.43, 0.46) * mm});
            skLineSegment(sketch, "E366", {"start": v(69.06, 0.49) * mm, "end": v(69.1, 0.48) * mm});
            skLineSegment(sketch, "E367", {"start": v(69.07, 0.49) * mm, "end": v(69.06, 0.49) * mm});
            skLineSegment(sketch, "E368", {"start": v(68.65, 0.56) * mm, "end": v(68.25, 0.66) * mm});
            skLineSegment(sketch, "E369", {"start": v(69.07, 0.49) * mm, "end": v(68.65, 0.56) * mm});
            skLineSegment(sketch, "E370", {"start": v(68.19, 0.67) * mm, "end": v(68.25, 0.66) * mm});
            skLineSegment(sketch, "E371", {"start": v(68.19, 0.67) * mm, "end": v(68.19, 0.67) * mm});
            skLineSegment(sketch, "E372", {"start": v(67.9, 0.77) * mm, "end": v(67.62, 0.87) * mm});
            skLineSegment(sketch, "E373", {"start": v(68.19, 0.67) * mm, "end": v(67.9, 0.77) * mm});
            skLineSegment(sketch, "E374", {"start": v(67.62, 0.87) * mm, "end": v(67.58, 0.88) * mm});
            skLineSegment(sketch, "E375", {"start": v(67.58, 0.88) * mm, "end": v(67.43, 0.95) * mm});
            skLineSegment(sketch, "E376", {"start": v(67.43, 0.95) * mm, "end": v(67.4, 0.96) * mm});
            skLineSegment(sketch, "E377", {"start": v(67.4, 0.96) * mm, "end": v(67.39, 0.97) * mm});
            skLineSegment(sketch, "E378", {"start": v(67.39, 0.97) * mm, "end": v(67.3, 1.01) * mm});
            skLineSegment(sketch, "E379", {"start": v(67.3, 1.01) * mm, "end": v(67.02, 1.16) * mm});
            skLineSegment(sketch, "E380", {"start": v(67.02, 1.16) * mm, "end": v(67, 1.16) * mm});
            skLineSegment(sketch, "E381", {"start": v(67, 1.16) * mm, "end": v(66.93, 1.2) * mm});
            skLineSegment(sketch, "E382", {"start": v(66.93, 1.2) * mm, "end": v(66.89, 1.24) * mm});
            skLineSegment(sketch, "E383", {"start": v(66.89, 1.24) * mm, "end": v(66.75, 1.33) * mm});
            skLineSegment(sketch, "E384", {"start": v(66.75, 1.33) * mm, "end": v(66.48, 1.51) * mm});
            skLineSegment(sketch, "E385", {"start": v(66.34, 1.61) * mm, "end": v(66.24, 1.7) * mm});
            skLineSegment(sketch, "E386", {"start": v(66.48, 1.51) * mm, "end": v(66.34, 1.61) * mm});
            skLineSegment(sketch, "E387", {"start": v(66.24, 1.7) * mm, "end": v(66.23, 1.7) * mm});
            skLineSegment(sketch, "E388", {"start": v(66.1, 1.82) * mm, "end": v(65.99, 1.92) * mm});
            skLineSegment(sketch, "E389", {"start": v(66.23, 1.7) * mm, "end": v(66.1, 1.82) * mm});
            skLineSegment(sketch, "E390", {"start": v(65.86, 2.04) * mm, "end": v(65.99, 1.92) * mm});
            skLineSegment(sketch, "E391", {"start": v(65.86, 2.04) * mm, "end": v(65.86, 2.04) * mm});
            skLineSegment(sketch, "E392", {"start": v(65.86, 2.04) * mm, "end": v(65.67, 2.25) * mm});
            skLineSegment(sketch, "E393", {"start": v(65.66, 2.25) * mm, "end": v(65.67, 2.25) * mm});
            skLineSegment(sketch, "E394", {"start": v(65.5, 2.43) * mm, "end": v(65.66, 2.25) * mm});
            skLineSegment(sketch, "E395", {"start": v(66.38, 2.33) * mm, "end": v(65.5, 2.43) * mm});
            skLineSegment(sketch, "E396", {"start": v(67.32, 2.38) * mm, "end": v(67.66, 2.49) * mm});
            skLineSegment(sketch, "E397", {"start": v(67.01, 2.32) * mm, "end": v(67.32, 2.38) * mm});
            skLineSegment(sketch, "E398", {"start": v(66.7, 2.31) * mm, "end": v(67.01, 2.32) * mm});
            skLineSegment(sketch, "E399", {"start": v(66.38, 2.33) * mm, "end": v(66.7, 2.31) * mm});
            skLineSegment(sketch, "E400", {"start": v(68.41, 2.87) * mm, "end": v(67.66, 2.49) * mm});
            skLineSegment(sketch, "E401", {"start": v(68.41, 2.87) * mm, "end": v(68.6, 2.99) * mm});
            skLineSegment(sketch, "E402", {"start": v(68.6, 2.99) * mm, "end": v(68.83, 3.14) * mm});
            skLineSegment(sketch, "E403", {"start": v(68.83, 3.14) * mm, "end": v(68.88, 3.17) * mm});
            skLineSegment(sketch, "E404", {"start": v(68.88, 3.17) * mm, "end": v(68.88, 3.17) * mm});
            skLineSegment(sketch, "E405", {"start": v(68.88, 3.17) * mm, "end": v(68.9, 3.18) * mm});
            skLineSegment(sketch, "E406", {"start": v(68.9, 3.18) * mm, "end": v(68.9, 3.18) * mm});
            skLineSegment(sketch, "E407", {"start": v(69.15, 3.37) * mm, "end": v(69.34, 3.54) * mm});
            skLineSegment(sketch, "E408", {"start": v(68.9, 3.18) * mm, "end": v(69.15, 3.37) * mm});
            skLineSegment(sketch, "E409", {"start": v(69.34, 3.55) * mm, "end": v(69.34, 3.54) * mm});
            skLineSegment(sketch, "E410", {"start": v(69.47, 3.7) * mm, "end": v(69.34, 3.55) * mm});
            skLineSegment(sketch, "E411", {"start": v(69.68, 3.97) * mm, "end": v(69.47, 3.7) * mm});
            skLineSegment(sketch, "E412", {"start": v(69.72, 4) * mm, "end": v(69.68, 3.97) * mm});
            skLineSegment(sketch, "E413", {"start": v(69.72, 4) * mm, "end": v(69.9, 4.36) * mm});
            skLineSegment(sketch, "E414", {"start": v(69.97, 4.54) * mm, "end": v(69.9, 4.36) * mm});
            skLineSegment(sketch, "E415", {"start": v(69.97, 4.54) * mm, "end": v(69.97, 4.56) * mm});
            skLineSegment(sketch, "E416", {"start": v(70.08, 4.85) * mm, "end": v(70.14, 5.08) * mm});
            skLineSegment(sketch, "E417", {"start": v(69.97, 4.56) * mm, "end": v(70.08, 4.85) * mm});
            skLineSegment(sketch, "E418", {"start": v(70.14, 5.08) * mm, "end": v(70.15, 5.12) * mm});
            skLineSegment(sketch, "E419", {"start": v(70.21, 5.38) * mm, "end": v(70.15, 5.12) * mm});
            skLineSegment(sketch, "E420", {"start": v(70.21, 5.38) * mm, "end": v(70.25, 5.71) * mm});
            skLineSegment(sketch, "E421", {"start": v(70.25, 5.96) * mm, "end": v(70.25, 5.71) * mm});
            skLineSegment(sketch, "E422", {"start": v(70.23, 6.2) * mm, "end": v(70.2, 6.38) * mm});
            skLineSegment(sketch, "E423", {"start": v(70.25, 5.96) * mm, "end": v(70.23, 6.2) * mm});
            skLineSegment(sketch, "E424", {"start": v(70.2, 6.38) * mm, "end": v(70.2, 6.4) * mm});
            skLineSegment(sketch, "E425", {"start": v(70.2, 6.4) * mm, "end": v(70.2, 6.4) * mm});
            skLineSegment(sketch, "E426", {"start": v(70.2, 6.4) * mm, "end": v(70.12, 6.77) * mm});
            skLineSegment(sketch, "E427", {"start": v(70.12, 6.77) * mm, "end": v(70.08, 6.9) * mm});
            skLineSegment(sketch, "E428", {"start": v(70.08, 6.9) * mm, "end": v(69.96, 7.24) * mm});
            skLineSegment(sketch, "E429", {"start": v(69.86, 7.47) * mm, "end": v(69.77, 7.64) * mm});
            skLineSegment(sketch, "E430", {"start": v(69.96, 7.24) * mm, "end": v(69.86, 7.47) * mm});
            skLineSegment(sketch, "E431", {"start": v(69.63, 7.84) * mm, "end": v(69.77, 7.64) * mm});
            skLineSegment(sketch, "E432", {"start": v(69.63, 7.84) * mm, "end": v(69.63, 7.84) * mm});
            skLineSegment(sketch, "E433", {"start": v(69.52, 7.98) * mm, "end": v(69.42, 8.08) * mm});
            skLineSegment(sketch, "E434", {"start": v(69.63, 7.84) * mm, "end": v(69.52, 7.98) * mm});
            skLineSegment(sketch, "E435", {"start": v(69.42, 8.08) * mm, "end": v(69.2, 8.3) * mm});
            skLineSegment(sketch, "E436", {"start": v(69.09, 8.4) * mm, "end": v(69.2, 8.3) * mm});
            skLineSegment(sketch, "E437", {"start": v(69.09, 8.4) * mm, "end": v(68.88, 8.57) * mm});
            skLineSegment(sketch, "E438", {"start": v(68.79, 8.63) * mm, "end": v(68.88, 8.57) * mm});
            skLineSegment(sketch, "E439", {"start": v(68.53, 6.96) * mm, "end": v(68.5, 6.99) * mm});
            skLineSegment(sketch, "E440", {"start": v(68.5, 6.99) * mm, "end": v(68.42, 7.17) * mm});
            skLineSegment(sketch, "E441", {"start": v(68.42, 7.17) * mm, "end": v(68.3, 7.33) * mm});
            skLineSegment(sketch, "E442", {"start": v(68.3, 7.33) * mm, "end": v(68.17, 7.46) * mm});
            skLineSegment(sketch, "E443", {"start": v(68.17, 7.46) * mm, "end": v(68.02, 7.57) * mm});
            skLineSegment(sketch, "E444", {"start": v(68.02, 7.57) * mm, "end": v(67.85, 7.65) * mm});
            skLineSegment(sketch, "E445", {"start": v(67.85, 7.65) * mm, "end": v(67.66, 7.71) * mm});
            skLineSegment(sketch, "E446", {"start": v(67.66, 7.71) * mm, "end": v(67.25, 7.75) * mm});
            skLineSegment(sketch, "E447", {"start": v(67.25, 7.75) * mm, "end": v(67.2, 7.76) * mm});
            skLineSegment(sketch, "E448", {"start": v(67.2, 7.76) * mm, "end": v(67.14, 7.75) * mm});
            skLineSegment(sketch, "E449", {"start": v(67.14, 7.75) * mm, "end": v(66.9, 7.7) * mm});
            skLineSegment(sketch, "E450", {"start": v(66.9, 7.7) * mm, "end": v(66.66, 7.6) * mm});
            skLineSegment(sketch, "E451", {"start": v(66.66, 7.6) * mm, "end": v(66.64, 7.6) * mm});
            skLineSegment(sketch, "E452", {"start": v(66.64, 7.6) * mm, "end": v(66.63, 7.6) * mm});
            skLineSegment(sketch, "E453", {"start": v(66.63, 7.6) * mm, "end": v(66.42, 7.45) * mm});
            skLineSegment(sketch, "E454", {"start": v(66.42, 7.45) * mm, "end": v(66.26, 7.28) * mm});
            skLineSegment(sketch, "E455", {"start": v(66.26, 7.28) * mm, "end": v(66.12, 7.08) * mm});
            skLineSegment(sketch, "E456", {"start": v(66.12, 7.08) * mm, "end": v(66.11, 7.08) * mm});
            skLineSegment(sketch, "E457", {"start": v(66.11, 7.08) * mm, "end": v(66.09, 7) * mm});
            skLineSegment(sketch, "E458", {"start": v(66.09, 7) * mm, "end": v(66.03, 6.85) * mm});
            skLineSegment(sketch, "E459", {"start": v(66.03, 6.85) * mm, "end": v(66.03, 6.85) * mm});
            skLineSegment(sketch, "E460", {"start": v(66.03, 6.85) * mm, "end": v(65.99, 6.65) * mm});
            skLineSegment(sketch, "E461", {"start": v(65.99, 6.65) * mm, "end": v(65.97, 6.64) * mm});
            skLineSegment(sketch, "E462", {"start": v(65.97, 6.64) * mm, "end": v(65.97, 6.47) * mm});
            skLineSegment(sketch, "E463", {"start": v(65.97, 6.47) * mm, "end": v(68.2, 6.47) * mm});
            skLineSegment(sketch, "E464", {"start": v(68.2, 6.47) * mm, "end": v(68.2, 5.37) * mm});
            skLineSegment(sketch, "E465", {"start": v(68.1, 5.37) * mm, "end": v(68.2, 5.37) * mm});
            skLineSegment(sketch, "E466", {"start": v(68.1, 5.37) * mm, "end": v(67.76, 5.37) * mm});
            skLineSegment(sketch, "E467", {"start": v(67.76, 5.37) * mm, "end": v(67.76, 5.37) * mm});
            skLineSegment(sketch, "E468", {"start": v(67.12, 5.37) * mm, "end": v(67.76, 5.37) * mm});
            skLineSegment(sketch, "E469", {"start": v(67.12, 5.37) * mm, "end": v(67.12, 5.37) * mm});
            skLineSegment(sketch, "E470", {"start": v(67.12, 5.37) * mm, "end": v(64.36, 5.37) * mm});
            skLineSegment(sketch, "E471", {"start": v(64.36, 5.4) * mm, "end": v(64.35, 5.6) * mm});
            skLineSegment(sketch, "E472", {"start": v(64.37, 5.9) * mm, "end": v(64.36, 5.73) * mm});
            skLineSegment(sketch, "E473", {"start": v(64.36, 5.73) * mm, "end": v(64.35, 5.6) * mm});
            skLineSegment(sketch, "E474", {"start": v(64.42, 6.19) * mm, "end": v(64.37, 5.9) * mm});
            skLineSegment(sketch, "E475", {"start": v(64.42, 6.19) * mm, "end": v(64.42, 6.19) * mm});
            skLineSegment(sketch, "E476", {"start": v(64.42, 6.19) * mm, "end": v(64.45, 6.4) * mm});
            skLineSegment(sketch, "E477", {"start": v(64.47, 6.46) * mm, "end": v(64.45, 6.4) * mm});
            skLineSegment(sketch, "E478", {"start": v(64.52, 6.65) * mm, "end": v(64.47, 6.46) * mm});
            skLineSegment(sketch, "E479", {"start": v(64.54, 6.74) * mm, "end": v(64.52, 6.65) * mm});
            skLineSegment(sketch, "E480", {"start": v(64.55, 6.76) * mm, "end": v(64.54, 6.74) * mm});
            skLineSegment(sketch, "E481", {"start": v(64.55, 6.77) * mm, "end": v(64.55, 6.76) * mm});
            skLineSegment(sketch, "E482", {"start": v(64.56, 6.8) * mm, "end": v(64.55, 6.77) * mm});
            skLineSegment(sketch, "E483", {"start": v(64.56, 6.81) * mm, "end": v(64.56, 6.8) * mm});
            skLineSegment(sketch, "E484", {"start": v(64.6, 6.9) * mm, "end": v(64.56, 6.81) * mm});
            skLineSegment(sketch, "E485", {"start": v(64.68, 7.15) * mm, "end": v(64.63, 7.02) * mm});
            skLineSegment(sketch, "E486", {"start": v(64.63, 7.02) * mm, "end": v(64.6, 6.9) * mm});
            skLineSegment(sketch, "E487", {"start": v(64.68, 7.16) * mm, "end": v(64.68, 7.15) * mm});
            skLineSegment(sketch, "E488", {"start": v(67.34, 9) * mm, "end": v(67.34, 9) * mm});
            skLineSegment(sketch, "E489", {"start": v(74, 9.42) * mm, "end": v(74.02, 9.4) * mm});
            skLineSegment(sketch, "E490", {"start": v(67.34, 9) * mm, "end": v(67.62, 9) * mm});
            skLineSegment(sketch, "E491", {"start": v(74, 9.42) * mm, "end": v(74, 9.43) * mm});
            skLineSegment(sketch, "E492", {"start": v(67.93, 8.94) * mm, "end": v(67.62, 9) * mm});
            skLineSegment(sketch, "E493", {"start": v(74, 9.43) * mm, "end": v(73.92, 9.51) * mm});
            skLineSegment(sketch, "E494", {"start": v(67.93, 8.94) * mm, "end": v(68.1, 8.9) * mm});
            skLineSegment(sketch, "E495", {"start": v(73.64, 9.83) * mm, "end": v(73.92, 9.51) * mm});
            skLineSegment(sketch, "E496", {"start": v(68.45, 8.78) * mm, "end": v(68.22, 8.86) * mm});
            skLineSegment(sketch, "E497", {"start": v(73.64, 9.83) * mm, "end": v(73.64, 9.84) * mm});
            skLineSegment(sketch, "E498", {"start": v(73.64, 9.84) * mm, "end": v(73.5, 9.96) * mm});
            skLineSegment(sketch, "E499", {"start": v(74.18, 9.2) * mm, "end": v(74.3, 9.03) * mm});
            skLineSegment(sketch, "E500", {"start": v(68.79, 8.63) * mm, "end": v(68.6, 8.72) * mm});
            skLineSegment(sketch, "E501", {"start": v(73.25, 10.17) * mm, "end": v(73.4, 10.06) * mm});
            skLineSegment(sketch, "E502", {"start": v(73.4, 10.06) * mm, "end": v(73.5, 9.96) * mm});
            skLineSegment(sketch, "E503", {"start": v(73.23, 10.18) * mm, "end": v(73.25, 10.17) * mm});
            skLineSegment(sketch, "E504", {"start": v(73.23, 10.18) * mm, "end": v(73.23, 10.19) * mm});
            skLineSegment(sketch, "E505", {"start": v(73.23, 10.19) * mm, "end": v(73.02, 10.34) * mm});
            skLineSegment(sketch, "E506", {"start": v(72.2, 10.87) * mm, "end": v(72.2, 10.86) * mm});
            skLineSegment(sketch, "E507", {"start": v(71.66, 11.1) * mm, "end": v(71.97, 10.98) * mm});
            skLineSegment(sketch, "E508", {"start": v(71.1, 11.27) * mm, "end": v(71.66, 11.1) * mm});
            skLineSegment(sketch, "E509", {"start": v(72.41, 10.75) * mm, "end": v(72.2, 10.87) * mm});
            skLineSegment(sketch, "E510", {"start": v(72.4, 10.75) * mm, "end": v(72.41, 10.75) * mm});
            skLineSegment(sketch, "E511", {"start": v(72.4, 10.75) * mm, "end": v(72.62, 10.62) * mm});
            skLineSegment(sketch, "E512", {"start": v(72.83, 10.5) * mm, "end": v(72.62, 10.62) * mm});
            skLineSegment(sketch, "E513", {"start": v(72.83, 10.48) * mm, "end": v(72.83, 10.5) * mm});
            skLineSegment(sketch, "E514", {"start": v(72.83, 10.48) * mm, "end": v(73.02, 10.34) * mm});
            skLineSegment(sketch, "E515", {"start": v(68.22, 8.86) * mm, "end": v(68.1, 8.9) * mm});
            skLineSegment(sketch, "E516", {"start": v(74.02, 9.4) * mm, "end": v(74.18, 9.2) * mm});
            skLineSegment(sketch, "E517", {"start": v(67.34, 9) * mm, "end": v(67.05, 9) * mm});
            skLineSegment(sketch, "E518", {"start": v(71.97, 10.98) * mm, "end": v(72.2, 10.86) * mm});
            skCircle(sketch, "E519", {"center": v(72.79, 5.9) * mm, "radius": 0.7 * mm});
            skLineSegment(sketch, "E520", {"start": v(68.43, 4.6) * mm, "end": v(68.55, 4.84) * mm});
            skLineSegment(sketch, "E521", {"start": v(66.46, 8.87) * mm, "end": v(67.05, 9) * mm});
            skLineSegment(sketch, "E522", {"start": v(66.46, 8.87) * mm, "end": v(66.24, 8.8) * mm});
            skLineSegment(sketch, "E523", {"start": v(65.74, 8.53) * mm, "end": v(66.24, 8.8) * mm});
            skLineSegment(sketch, "E524", {"start": v(65.59, 8.42) * mm, "end": v(65.47, 8.33) * mm});
            skLineSegment(sketch, "E525", {"start": v(65.74, 8.53) * mm, "end": v(65.59, 8.42) * mm});
            skLineSegment(sketch, "E526", {"start": v(65.27, 8.13) * mm, "end": v(65.47, 8.33) * mm});
            skLineSegment(sketch, "E527", {"start": v(65.27, 8.13) * mm, "end": v(65.27, 8.13) * mm});
            skLineSegment(sketch, "E528", {"start": v(65.27, 8.13) * mm, "end": v(65.23, 8.08) * mm});
            skLineSegment(sketch, "E529", {"start": v(65.13, 7.96) * mm, "end": v(65.07, 7.86) * mm});
            skLineSegment(sketch, "E530", {"start": v(65.23, 8.08) * mm, "end": v(65.13, 7.96) * mm});
            skLineSegment(sketch, "E531", {"start": v(65.07, 7.86) * mm, "end": v(64.89, 7.57) * mm});
            skLineSegment(sketch, "E532", {"start": v(64.79, 7.4) * mm, "end": v(64.89, 7.57) * mm});
            skLineSegment(sketch, "E533", {"start": v(64.79, 7.4) * mm, "end": v(64.78, 7.37) * mm});
            skLineSegment(sketch, "E534", {"start": v(64.78, 7.37) * mm, "end": v(64.68, 7.16) * mm});
            skLineSegment(sketch, "E535", {"start": v(68.52, 6.96) * mm, "end": v(68.53, 6.96) * mm});
            skLineSegment(sketch, "E536", {"start": v(68.6, 6.75) * mm, "end": v(68.52, 6.96) * mm});
            skLineSegment(sketch, "E537", {"start": v(68.6, 6.75) * mm, "end": v(68.6, 6.75) * mm});
            skLineSegment(sketch, "E538", {"start": v(68.6, 6.68) * mm, "end": v(68.6, 6.75) * mm});
            skLineSegment(sketch, "E539", {"start": v(68.68, 6.32) * mm, "end": v(68.6, 6.68) * mm});
            skLineSegment(sketch, "E540", {"start": v(64.37, 7.16) * mm, "end": v(64.32, 6.89) * mm});
            skLineSegment(sketch, "E541", {"start": v(64.4, 7.29) * mm, "end": v(64.37, 7.16) * mm});
            skLineSegment(sketch, "E542", {"start": v(64.4, 7.28) * mm, "end": v(64.4, 7.29) * mm});
            skLineSegment(sketch, "E543", {"start": v(64.6, 7.92) * mm, "end": v(64.4, 7.28) * mm});
            skLineSegment(sketch, "E544", {"start": v(64.63, 7.99) * mm, "end": v(64.6, 7.92) * mm});
            skLineSegment(sketch, "E545", {"start": v(64.7, 8.17) * mm, "end": v(64.63, 7.99) * mm});
            skLineSegment(sketch, "E546", {"start": v(64.72, 8.2) * mm, "end": v(64.7, 8.17) * mm});
            skLineSegment(sketch, "E547", {"start": v(64.72, 8.2) * mm, "end": v(64.72, 8.2) * mm});
            skLineSegment(sketch, "E548", {"start": v(64.92, 8.6) * mm, "end": v(64.72, 8.2) * mm});
            skLineSegment(sketch, "E549", {"start": v(64.92, 8.6) * mm, "end": v(64.92, 8.6) * mm});
            skLineSegment(sketch, "E550", {"start": v(64.94, 8.63) * mm, "end": v(64.92, 8.6) * mm});
            skLineSegment(sketch, "E551", {"start": v(64.96, 8.67) * mm, "end": v(64.94, 8.63) * mm});
            skLineSegment(sketch, "E552", {"start": v(65.14, 8.94) * mm, "end": v(64.96, 8.67) * mm});
            skLineSegment(sketch, "E553", {"start": v(65.17, 8.98) * mm, "end": v(65.14, 8.94) * mm});
            skLineSegment(sketch, "E554", {"start": v(65.18, 9) * mm, "end": v(65.17, 8.98) * mm});
            skLineSegment(sketch, "E555", {"start": v(65.17, 9) * mm, "end": v(65.18, 9) * mm});
            skLineSegment(sketch, "E556", {"start": v(65.3, 9.2) * mm, "end": v(65.17, 9) * mm});
            skLineSegment(sketch, "E557", {"start": v(65.33, 9.2) * mm, "end": v(65.3, 9.2) * mm});
            skLineSegment(sketch, "E558", {"start": v(65.46, 9.38) * mm, "end": v(65.33, 9.2) * mm});
            skLineSegment(sketch, "E559", {"start": v(65.45, 9.38) * mm, "end": v(65.46, 9.38) * mm});
            skLineSegment(sketch, "E560", {"start": v(65.61, 9.57) * mm, "end": v(65.45, 9.38) * mm});
            skLineSegment(sketch, "E561", {"start": v(65.71, 9.69) * mm, "end": v(65.61, 9.57) * mm});
            skLineSegment(sketch, "E562", {"start": v(65.76, 9.74) * mm, "end": v(65.71, 9.69) * mm});
            skLineSegment(sketch, "E563", {"start": v(65.82, 9.8) * mm, "end": v(65.76, 9.74) * mm});
            skLineSegment(sketch, "E564", {"start": v(68.15, 11.2) * mm, "end": v(68.54, 11.3) * mm});
            skLineSegment(sketch, "E565", {"start": v(68.56, 11.31) * mm, "end": v(68.54, 11.3) * mm});
            skLineSegment(sketch, "E566", {"start": v(68.56, 11.31) * mm, "end": v(68.56, 11.31) * mm});
            skLineSegment(sketch, "E567", {"start": v(69.15, 11.41) * mm, "end": v(69.73, 11.45) * mm});
            skLineSegment(sketch, "E568", {"start": v(68.56, 11.31) * mm, "end": v(69.15, 11.41) * mm});
            skLineSegment(sketch, "E569", {"start": v(70.11, 11.43) * mm, "end": v(70.41, 11.4) * mm});
            skLineSegment(sketch, "E570", {"start": v(71.1, 11.27) * mm, "end": v(71.1, 11.28) * mm});
            skLineSegment(sketch, "E571", {"start": v(71.1, 11.28) * mm, "end": v(71.03, 11.29) * mm});
            skLineSegment(sketch, "E572", {"start": v(70.41, 11.4) * mm, "end": v(71.03, 11.29) * mm});
            skLineSegment(sketch, "E573", {"start": v(69.73, 11.45) * mm, "end": v(70.11, 11.43) * mm});
            skLineSegment(sketch, "E574", {"start": v(68.15, 11.2) * mm, "end": v(68.15, 11.2) * mm});
            skLineSegment(sketch, "E575", {"start": v(68.15, 11.2) * mm, "end": v(67.94, 11.14) * mm});
            skLineSegment(sketch, "E576", {"start": v(67.39, 10.91) * mm, "end": v(67.65, 11.03) * mm});
            skLineSegment(sketch, "E577", {"start": v(67.65, 11.03) * mm, "end": v(67.94, 11.14) * mm});
            skLineSegment(sketch, "E578", {"start": v(66.86, 10.62) * mm, "end": v(67.15, 10.8) * mm});
            skLineSegment(sketch, "E579", {"start": v(67.15, 10.8) * mm, "end": v(67.39, 10.91) * mm});
            skLineSegment(sketch, "E580", {"start": v(66.86, 10.62) * mm, "end": v(66.75, 10.55) * mm});
            skLineSegment(sketch, "E581", {"start": v(66.75, 10.55) * mm, "end": v(66.74, 10.54) * mm});
            skLineSegment(sketch, "E582", {"start": v(66.52, 10.4) * mm, "end": v(66.74, 10.54) * mm});
            skLineSegment(sketch, "E583", {"start": v(66.52, 10.4) * mm, "end": v(66.25, 10.17) * mm});
            skLineSegment(sketch, "E584", {"start": v(66.25, 10.17) * mm, "end": v(66, 9.97) * mm});
            skLineSegment(sketch, "E585", {"start": v(66, 9.97) * mm, "end": v(65.82, 9.8) * mm});
            skLineSegment(sketch, "E586", {"start": v(64.32, 6.89) * mm, "end": v(64.31, 6.89) * mm});
            skLineSegment(sketch, "E587", {"start": v(64.31, 6.89) * mm, "end": v(64.3, 6.84) * mm});
            skLineSegment(sketch, "E588", {"start": v(64.3, 6.84) * mm, "end": v(64.26, 6.52) * mm});
            skLineSegment(sketch, "E589", {"start": v(64.26, 6.52) * mm, "end": v(64.24, 6.27) * mm});
            skLineSegment(sketch, "E590", {"start": v(64.24, 6.27) * mm, "end": v(64.23, 5.98) * mm});
            skLineSegment(sketch, "E591", {"start": v(64.23, 5.98) * mm, "end": v(64.24, 5.82) * mm});
            skLineSegment(sketch, "E592", {"start": v(64.24, 5.82) * mm, "end": v(64.24, 5.7) * mm});
            skLineSegment(sketch, "E593", {"start": v(64.24, 5.7) * mm, "end": v(64.24, 5.7) * mm});
            skLineSegment(sketch, "E594", {"start": v(64.24, 5.7) * mm, "end": v(64.25, 5.41) * mm});
            skLineSegment(sketch, "E595", {"start": v(64.25, 5.41) * mm, "end": v(64.27, 5.25) * mm});
            skLineSegment(sketch, "E596", {"start": v(64.27, 5.25) * mm, "end": v(64.3, 5.12) * mm});
            skLineSegment(sketch, "E597", {"start": v(64.3, 5.12) * mm, "end": v(64.3, 5.12) * mm});
            skLineSegment(sketch, "E598", {"start": v(64.3, 5.12) * mm, "end": v(64.3, 5.08) * mm});
            skLineSegment(sketch, "E599", {"start": v(64.3, 5.08) * mm, "end": v(64.34, 4.95) * mm});
            skLineSegment(sketch, "E600", {"start": v(64.34, 4.95) * mm, "end": v(64.38, 4.86) * mm});
            skLineSegment(sketch, "E601", {"start": v(64.38, 4.86) * mm, "end": v(64.39, 4.84) * mm});
            skLineSegment(sketch, "E602", {"start": v(64.39, 4.84) * mm, "end": v(64.52, 4.6) * mm});
            skLineSegment(sketch, "E603", {"start": v(64.52, 4.6) * mm, "end": v(64.6, 4.47) * mm});
            skLineSegment(sketch, "E604", {"start": v(64.6, 4.47) * mm, "end": v(64.64, 4.43) * mm});
            skLineSegment(sketch, "E605", {"start": v(64.64, 4.43) * mm, "end": v(64.64, 4.43) * mm});
            skLineSegment(sketch, "E606", {"start": v(64.64, 4.43) * mm, "end": v(64.9, 4.16) * mm});
            skLineSegment(sketch, "E607", {"start": v(64.9, 4.16) * mm, "end": v(65.15, 3.98) * mm});
            skLineSegment(sketch, "E608", {"start": v(65.15, 3.98) * mm, "end": v(65.19, 3.95) * mm});
            skLineSegment(sketch, "E609", {"start": v(65.19, 3.95) * mm, "end": v(65.2, 3.94) * mm});
            skLineSegment(sketch, "E610", {"start": v(65.2, 3.94) * mm, "end": v(65.2, 3.94) * mm});
            skLineSegment(sketch, "E611", {"start": v(65.2, 3.94) * mm, "end": v(65.6, 3.74) * mm});
            skLineSegment(sketch, "E612", {"start": v(65.6, 3.74) * mm, "end": v(65.76, 3.68) * mm});
            skLineSegment(sketch, "E613", {"start": v(65.76, 3.68) * mm, "end": v(65.96, 3.63) * mm});
            skLineSegment(sketch, "E614", {"start": v(65.96, 3.63) * mm, "end": v(66.07, 3.6) * mm});
            skLineSegment(sketch, "E615", {"start": v(66.07, 3.6) * mm, "end": v(66.16, 3.6) * mm});
            skLineSegment(sketch, "E616", {"start": v(66.16, 3.6) * mm, "end": v(66.33, 3.58) * mm});
            skLineSegment(sketch, "E617", {"start": v(66.33, 3.58) * mm, "end": v(66.63, 3.58) * mm});
            skLineSegment(sketch, "E618", {"start": v(66.63, 3.58) * mm, "end": v(66.83, 3.6) * mm});
            skLineSegment(sketch, "E619", {"start": v(66.83, 3.6) * mm, "end": v(66.88, 3.61) * mm});
            skLineSegment(sketch, "E620", {"start": v(66.88, 3.61) * mm, "end": v(67.19, 3.69) * mm});
            skLineSegment(sketch, "E621", {"start": v(67.19, 3.69) * mm, "end": v(67.46, 3.79) * mm});
            skLineSegment(sketch, "E622", {"start": v(67.46, 3.79) * mm, "end": v(67.48, 3.8) * mm});
            skLineSegment(sketch, "E623", {"start": v(67.48, 3.8) * mm, "end": v(67.67, 3.9) * mm});
            skLineSegment(sketch, "E624", {"start": v(67.67, 3.9) * mm, "end": v(67.7, 3.9) * mm});
            skLineSegment(sketch, "E625", {"start": v(67.7, 3.9) * mm, "end": v(67.78, 3.96) * mm});
            skLineSegment(sketch, "E626", {"start": v(67.78, 3.96) * mm, "end": v(68.02, 4.14) * mm});
            skLineSegment(sketch, "E627", {"start": v(68.02, 4.14) * mm, "end": v(68.32, 4.46) * mm});
            skLineSegment(sketch, "E628", {"start": v(68.32, 4.46) * mm, "end": v(68.35, 4.47) * mm});
            skLineSegment(sketch, "E629", {"start": v(68.35, 4.47) * mm, "end": v(68.43, 4.6) * mm});
            skLineSegment(sketch, "E630", {"start": v(68.55, 4.84) * mm, "end": v(68.63, 5.07) * mm});
            skLineSegment(sketch, "E631", {"start": v(68.63, 5.07) * mm, "end": v(68.68, 5.32) * mm});
            skLineSegment(sketch, "E632", {"start": v(68.68, 5.32) * mm, "end": v(68.7, 5.58) * mm});
            skLineSegment(sketch, "E633", {"start": v(68.7, 5.58) * mm, "end": v(68.7, 5.95) * mm});
            skLineSegment(sketch, "E634", {"start": v(68.7, 5.95) * mm, "end": v(68.68, 6.32) * mm});
            skLineSegment(sketch, "E635", {"start": v(68.6, 8.72) * mm, "end": v(68.45, 8.78) * mm});
            skSolve(sketch);
        }
        {
            var Q0;
            Q0 = qSketchRegion(id + "F9", true);
            extrude(context, id + "F10", {"entities" : qUnion([Q0]), "operationType" : NewBodyOperationType.REMOVE, "oppositeDirection" : true, "depth" : 1 * mm, "offsetDistance" : 25 * mm});
        }
    });
